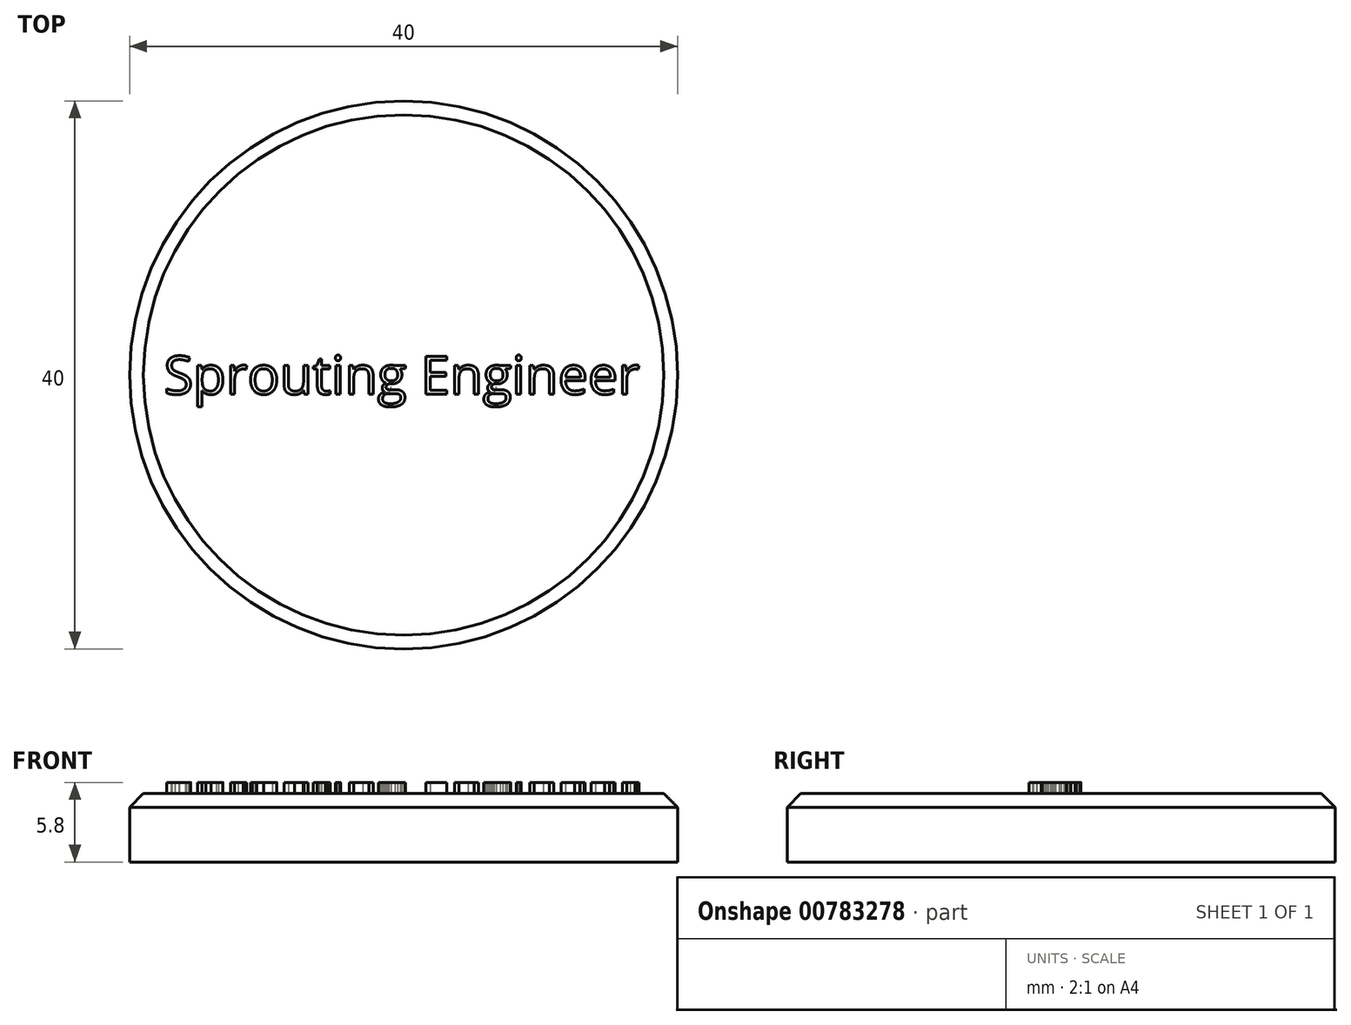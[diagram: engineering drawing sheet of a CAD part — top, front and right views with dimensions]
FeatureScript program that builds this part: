
annotation { "Feature Type Name" : "Feature", "Feature Type Description" : "" }
export const myFeature = defineFeature(function(context is Context, id is Id, definition is map)
    precondition{}
    {
        {
            var Q0;
            Q0=qCreatedBy(makeId("Top.planeOp"),FACE);
            var sketch = newSketch(context, id + "F0", { "sketchPlane" : qUnion([Q0])});
            skCircle(sketch, "E0", {"center": v(0, 0) * mm, "radius": 20 * mm});
            skLineSegment(sketch, "E1", {"start": v(-2.13, 19.89) * mm, "end": v(-1, 23) * mm});
            skLineSegment(sketch, "E2", {"start": v(-1, 23) * mm, "end": v(1, 23) * mm});
            skLineSegment(sketch, "E3", {"start": v(1, 23) * mm, "end": v(2.13, 19.89) * mm});
            skSolve(sketch);
        }
        {
            var Q0;
            {var subQ0=sQuery(id+"F0.wireOp",EDGE,"E0");var subQ1=makeQuery(id+"F0.imprint","INTERSECT",VERTEX,{"derivedFrom":[subQ0,sQuery(id+"F0.wireOp",EDGE,"E1")]});Q0=makeQuery(id+"F0.imprint","IMPRINT",FACE,{"disambiguationData":[TD([[makeQuery(id+"F0.imprint","IMPRINT",EDGE,{"disambiguationData":[TD([[subQ1,1.0]])],"derivedFrom":subQ0}),1.0]])]});}
            var Q1;
            {var subQ0=sQuery(id+"F0.wireOp",EDGE,"E1");Q1=makeQuery(id+"F0.imprint","IMPRINT",FACE,{"disambiguationData":[TD([[makeQuery(id+"F0.imprint","IMPRINT",EDGE,{"derivedFrom":subQ0}),-1.0]])]});}
            extrude(context, id + "F1", {"entities" : qUnion([Q0, Q1]), "depth" : 5 * mm, "offsetDistance" : 25 * mm});
        }
        {
            var Q0;
            Q0=makeQuery(id+"F1.opExtrude","SWEPT_BODY",BODY,{"disambiguationData":[OSD([sQuery(id+"F0.wireOp",EDGE,"E0"),sQuery(id+"F0.wireOp",EDGE,"E1"),sQuery(id+"F0.wireOp",EDGE,"E2"),sQuery(id+"F0.wireOp",EDGE,"E3")])]});
            var Q1;
            Q1=sQuery(id+"F0.wireOp",EDGE,"E0");
            circularPattern(context, id + "F2", {"operationType" : NewBodyOperationType.ADD, "entities" : qUnion([Q0]), "axis" : qUnion([Q1]), "angle" : 360 * degree, "instanceCount" : 18, "equalSpace" : true});
        }
        {
            var Q0;
            Q0=makeQuery(id+"F1.opExtrude","CAP_FACE",FACE,{"disambiguationData":[OSD([sQuery(id+"F0.wireOp",EDGE,"E0"),sQuery(id+"F0.wireOp",EDGE,"E1"),sQuery(id+"F0.wireOp",EDGE,"E2"),sQuery(id+"F0.wireOp",EDGE,"E3")])],"isStart":false});
            var sketch = newSketch(context, id + "F3", { "sketchPlane" : qUnion([Q0])});
            skText(sketch, "E4", { "text": "Sprouting Engineer", "fontName": "OpenSans-Regular.ttf"});
            const initialGuessF3  = {"E4": [-0.0175, -0.0014, 1, 0, 0.0028]};
            skSetInitialGuess(sketch, initialGuessF3);
            skSolve(sketch);
        }
        {
            var Q0;
            Q0=qSketchRegion(id+"F3",true);
            extrude(context, id + "F4", {"entities" : qUnion([Q0]), "operationType" : NewBodyOperationType.ADD, "depth" : 0.8 * mm, "offsetDistance" : 25 * mm});
        }
        {
            var Q0;
            {var subQ1=sQuery(id+"F0.wireOp",EDGE,"E1");var subQ2=sQuery(id+"F0.wireOp",EDGE,"E0");Q0=makeQuery(id+"F2.boolean.opBoolean","SPLIT",EDGE,{"disambiguationData":[TD([makeQuery(id+"F2.opPattern","COPY",FACE,{"derivedFrom":makeQuery(id+"F1.opExtrude","SWEPT_FACE",FACE,{"disambiguationData":[OSD([subQ1])]}),"instanceName":"12"})])],"derivedFrom":makeQuery(id+"F1.opExtrude","CAP_EDGE",EDGE,{"disambiguationData":[OSD([subQ2])],"isStart":false})});}
            var Q1;
            Q1=makeQuery(id+"F2.opPattern","COPY",EDGE,{"derivedFrom":makeQuery(id+"F1.opExtrude","CAP_EDGE",EDGE,{"disambiguationData":[OSD([sQuery(id+"F0.wireOp",EDGE,"E1")])],"isStart":false}),"instanceName":"12"});
            var Q2;
            Q2=makeQuery(id+"F2.opPattern","COPY",EDGE,{"derivedFrom":makeQuery(id+"F1.opExtrude","CAP_EDGE",EDGE,{"disambiguationData":[OSD([sQuery(id+"F0.wireOp",EDGE,"E2")])],"isStart":false}),"instanceName":"12"});
            var Q3;
            Q3=makeQuery(id+"F2.opPattern","COPY",EDGE,{"derivedFrom":makeQuery(id+"F1.opExtrude","CAP_EDGE",EDGE,{"disambiguationData":[OSD([sQuery(id+"F0.wireOp",EDGE,"E3")])],"isStart":false}),"instanceName":"12"});
            var Q4;
            {var subQ1=sQuery(id+"F0.wireOp",EDGE,"E1");var subQ2=sQuery(id+"F0.wireOp",EDGE,"E0");Q4=makeQuery(id+"F2.boolean.opBoolean","SPLIT",EDGE,{"disambiguationData":[TD([makeQuery(id+"F2.opPattern","COPY",FACE,{"derivedFrom":makeQuery(id+"F1.opExtrude","SWEPT_FACE",FACE,{"disambiguationData":[OSD([subQ1])]}),"instanceName":"11"})])],"derivedFrom":makeQuery(id+"F1.opExtrude","CAP_EDGE",EDGE,{"disambiguationData":[OSD([subQ2])],"isStart":false})});}
            var Q5;
            Q5=makeQuery(id+"F2.opPattern","COPY",EDGE,{"derivedFrom":makeQuery(id+"F1.opExtrude","CAP_EDGE",EDGE,{"disambiguationData":[OSD([sQuery(id+"F0.wireOp",EDGE,"E1")])],"isStart":false}),"instanceName":"11"});
            var Q6;
            Q6=makeQuery(id+"F2.opPattern","COPY",EDGE,{"derivedFrom":makeQuery(id+"F1.opExtrude","CAP_EDGE",EDGE,{"disambiguationData":[OSD([sQuery(id+"F0.wireOp",EDGE,"E2")])],"isStart":false}),"instanceName":"11"});
            var Q7;
            Q7=makeQuery(id+"F2.opPattern","COPY",EDGE,{"derivedFrom":makeQuery(id+"F1.opExtrude","CAP_EDGE",EDGE,{"disambiguationData":[OSD([sQuery(id+"F0.wireOp",EDGE,"E3")])],"isStart":false}),"instanceName":"11"});
            var Q8;
            Q8=makeQuery(id+"F2.opPattern","COPY",EDGE,{"derivedFrom":makeQuery(id+"F1.opExtrude","CAP_EDGE",EDGE,{"disambiguationData":[OSD([sQuery(id+"F0.wireOp",EDGE,"E3")])],"isStart":false}),"instanceName":"13"});
            var Q9;
            Q9=makeQuery(id+"F2.opPattern","COPY",EDGE,{"derivedFrom":makeQuery(id+"F1.opExtrude","CAP_EDGE",EDGE,{"disambiguationData":[OSD([sQuery(id+"F0.wireOp",EDGE,"E2")])],"isStart":false}),"instanceName":"13"});
            var Q10;
            Q10=makeQuery(id+"F2.opPattern","COPY",EDGE,{"derivedFrom":makeQuery(id+"F1.opExtrude","CAP_EDGE",EDGE,{"disambiguationData":[OSD([sQuery(id+"F0.wireOp",EDGE,"E1")])],"isStart":false}),"instanceName":"13"});
            var Q11;
            {var subQ1=sQuery(id+"F0.wireOp",EDGE,"E1");var subQ2=sQuery(id+"F0.wireOp",EDGE,"E0");Q11=makeQuery(id+"F2.boolean.opBoolean","SPLIT",EDGE,{"disambiguationData":[TD([makeQuery(id+"F2.opPattern","COPY",FACE,{"derivedFrom":makeQuery(id+"F1.opExtrude","SWEPT_FACE",FACE,{"disambiguationData":[OSD([subQ1])]}),"instanceName":"13"})])],"derivedFrom":makeQuery(id+"F1.opExtrude","CAP_EDGE",EDGE,{"disambiguationData":[OSD([subQ2])],"isStart":false})});}
            var Q12;
            Q12=makeQuery(id+"F2.opPattern","COPY",EDGE,{"derivedFrom":makeQuery(id+"F1.opExtrude","CAP_EDGE",EDGE,{"disambiguationData":[OSD([sQuery(id+"F0.wireOp",EDGE,"E3")])],"isStart":false}),"instanceName":"14"});
            var Q13;
            Q13=makeQuery(id+"F2.opPattern","COPY",EDGE,{"derivedFrom":makeQuery(id+"F1.opExtrude","CAP_EDGE",EDGE,{"disambiguationData":[OSD([sQuery(id+"F0.wireOp",EDGE,"E2")])],"isStart":false}),"instanceName":"14"});
            var Q14;
            Q14=makeQuery(id+"F2.opPattern","COPY",EDGE,{"derivedFrom":makeQuery(id+"F1.opExtrude","CAP_EDGE",EDGE,{"disambiguationData":[OSD([sQuery(id+"F0.wireOp",EDGE,"E1")])],"isStart":false}),"instanceName":"14"});
            var Q15;
            {var subQ1=sQuery(id+"F0.wireOp",EDGE,"E1");var subQ2=sQuery(id+"F0.wireOp",EDGE,"E0");Q15=makeQuery(id+"F2.boolean.opBoolean","SPLIT",EDGE,{"disambiguationData":[TD([makeQuery(id+"F2.opPattern","COPY",FACE,{"derivedFrom":makeQuery(id+"F1.opExtrude","SWEPT_FACE",FACE,{"disambiguationData":[OSD([subQ1])]}),"instanceName":"14"})])],"derivedFrom":makeQuery(id+"F1.opExtrude","CAP_EDGE",EDGE,{"disambiguationData":[OSD([subQ2])],"isStart":false})});}
            var Q16;
            Q16=makeQuery(id+"F2.opPattern","COPY",EDGE,{"derivedFrom":makeQuery(id+"F1.opExtrude","CAP_EDGE",EDGE,{"disambiguationData":[OSD([sQuery(id+"F0.wireOp",EDGE,"E3")])],"isStart":false}),"instanceName":"15"});
            var Q17;
            Q17=makeQuery(id+"F2.opPattern","COPY",EDGE,{"derivedFrom":makeQuery(id+"F1.opExtrude","CAP_EDGE",EDGE,{"disambiguationData":[OSD([sQuery(id+"F0.wireOp",EDGE,"E2")])],"isStart":false}),"instanceName":"15"});
            var Q18;
            Q18=makeQuery(id+"F2.opPattern","COPY",EDGE,{"derivedFrom":makeQuery(id+"F1.opExtrude","CAP_EDGE",EDGE,{"disambiguationData":[OSD([sQuery(id+"F0.wireOp",EDGE,"E1")])],"isStart":false}),"instanceName":"15"});
            var Q19;
            {var subQ1=sQuery(id+"F0.wireOp",EDGE,"E1");var subQ2=sQuery(id+"F0.wireOp",EDGE,"E0");Q19=makeQuery(id+"F2.boolean.opBoolean","SPLIT",EDGE,{"disambiguationData":[TD([makeQuery(id+"F2.opPattern","COPY",FACE,{"derivedFrom":makeQuery(id+"F1.opExtrude","SWEPT_FACE",FACE,{"disambiguationData":[OSD([subQ1])]}),"instanceName":"15"})])],"derivedFrom":makeQuery(id+"F1.opExtrude","CAP_EDGE",EDGE,{"disambiguationData":[OSD([subQ2])],"isStart":false})});}
            var Q20;
            Q20=makeQuery(id+"F2.opPattern","COPY",EDGE,{"derivedFrom":makeQuery(id+"F1.opExtrude","CAP_EDGE",EDGE,{"disambiguationData":[OSD([sQuery(id+"F0.wireOp",EDGE,"E3")])],"isStart":false}),"instanceName":"16"});
            var Q21;
            Q21=makeQuery(id+"F2.opPattern","COPY",EDGE,{"derivedFrom":makeQuery(id+"F1.opExtrude","CAP_EDGE",EDGE,{"disambiguationData":[OSD([sQuery(id+"F0.wireOp",EDGE,"E2")])],"isStart":false}),"instanceName":"16"});
            var Q22;
            Q22=makeQuery(id+"F2.opPattern","COPY",EDGE,{"derivedFrom":makeQuery(id+"F1.opExtrude","CAP_EDGE",EDGE,{"disambiguationData":[OSD([sQuery(id+"F0.wireOp",EDGE,"E1")])],"isStart":false}),"instanceName":"16"});
            var Q23;
            {var subQ1=sQuery(id+"F0.wireOp",EDGE,"E1");var subQ2=sQuery(id+"F0.wireOp",EDGE,"E0");Q23=makeQuery(id+"F2.boolean.opBoolean","SPLIT",EDGE,{"disambiguationData":[TD([makeQuery(id+"F2.opPattern","COPY",FACE,{"derivedFrom":makeQuery(id+"F1.opExtrude","SWEPT_FACE",FACE,{"disambiguationData":[OSD([subQ1])]}),"instanceName":"16"})])],"derivedFrom":makeQuery(id+"F1.opExtrude","CAP_EDGE",EDGE,{"disambiguationData":[OSD([subQ2])],"isStart":false})});}
            var Q24;
            Q24=makeQuery(id+"F2.opPattern","COPY",EDGE,{"derivedFrom":makeQuery(id+"F1.opExtrude","CAP_EDGE",EDGE,{"disambiguationData":[OSD([sQuery(id+"F0.wireOp",EDGE,"E3")])],"isStart":false}),"instanceName":"17"});
            var Q25;
            Q25=makeQuery(id+"F2.opPattern","COPY",EDGE,{"derivedFrom":makeQuery(id+"F1.opExtrude","CAP_EDGE",EDGE,{"disambiguationData":[OSD([sQuery(id+"F0.wireOp",EDGE,"E1")])],"isStart":false}),"instanceName":"17"});
            var Q26;
            {var subQ0=sQuery(id+"F0.wireOp",EDGE,"E3");var subQ2=sQuery(id+"F0.wireOp",EDGE,"E0");Q26=makeQuery(id+"F2.boolean.opBoolean","SPLIT",EDGE,{"disambiguationData":[TD([makeQuery(id+"F1.opExtrude","SWEPT_FACE",FACE,{"disambiguationData":[OSD([subQ0])]})])],"derivedFrom":makeQuery(id+"F1.opExtrude","CAP_EDGE",EDGE,{"disambiguationData":[OSD([subQ2])],"isStart":false})});}
            var Q27;
            Q27=makeQuery(id+"F1.opExtrude","CAP_EDGE",EDGE,{"disambiguationData":[OSD([sQuery(id+"F0.wireOp",EDGE,"E3")])],"isStart":false});
            var Q28;
            Q28=makeQuery(id+"F1.opExtrude","CAP_EDGE",EDGE,{"disambiguationData":[OSD([sQuery(id+"F0.wireOp",EDGE,"E1")])],"isStart":false});
            var Q29;
            {var subQ1=sQuery(id+"F0.wireOp",EDGE,"E1");var subQ2=sQuery(id+"F0.wireOp",EDGE,"E0");Q29=makeQuery(id+"F2.boolean.opBoolean","SPLIT",EDGE,{"disambiguationData":[TD([makeQuery(id+"F1.opExtrude","SWEPT_FACE",FACE,{"disambiguationData":[OSD([subQ1])]})])],"derivedFrom":makeQuery(id+"F1.opExtrude","CAP_EDGE",EDGE,{"disambiguationData":[OSD([subQ2])],"isStart":false})});}
            var Q30;
            Q30=makeQuery(id+"F2.opPattern","COPY",EDGE,{"derivedFrom":makeQuery(id+"F1.opExtrude","CAP_EDGE",EDGE,{"disambiguationData":[OSD([sQuery(id+"F0.wireOp",EDGE,"E3")])],"isStart":false}),"instanceName":"1"});
            var Q31;
            Q31=makeQuery(id+"F2.opPattern","COPY",EDGE,{"derivedFrom":makeQuery(id+"F1.opExtrude","CAP_EDGE",EDGE,{"disambiguationData":[OSD([sQuery(id+"F0.wireOp",EDGE,"E1")])],"isStart":false}),"instanceName":"1"});
            var Q32;
            {var subQ1=sQuery(id+"F0.wireOp",EDGE,"E1");var subQ2=sQuery(id+"F0.wireOp",EDGE,"E0");Q32=makeQuery(id+"F2.boolean.opBoolean","SPLIT",EDGE,{"disambiguationData":[TD([makeQuery(id+"F2.opPattern","COPY",FACE,{"derivedFrom":makeQuery(id+"F1.opExtrude","SWEPT_FACE",FACE,{"disambiguationData":[OSD([subQ1])]}),"instanceName":"1"})])],"derivedFrom":makeQuery(id+"F1.opExtrude","CAP_EDGE",EDGE,{"disambiguationData":[OSD([subQ2])],"isStart":false})});}
            var Q33;
            Q33=makeQuery(id+"F2.opPattern","COPY",EDGE,{"derivedFrom":makeQuery(id+"F1.opExtrude","CAP_EDGE",EDGE,{"disambiguationData":[OSD([sQuery(id+"F0.wireOp",EDGE,"E3")])],"isStart":false}),"instanceName":"2"});
            var Q34;
            Q34=makeQuery(id+"F2.opPattern","COPY",EDGE,{"derivedFrom":makeQuery(id+"F1.opExtrude","CAP_EDGE",EDGE,{"disambiguationData":[OSD([sQuery(id+"F0.wireOp",EDGE,"E1")])],"isStart":false}),"instanceName":"2"});
            var Q35;
            {var subQ1=sQuery(id+"F0.wireOp",EDGE,"E1");var subQ2=sQuery(id+"F0.wireOp",EDGE,"E0");Q35=makeQuery(id+"F2.boolean.opBoolean","SPLIT",EDGE,{"disambiguationData":[TD([makeQuery(id+"F2.opPattern","COPY",FACE,{"derivedFrom":makeQuery(id+"F1.opExtrude","SWEPT_FACE",FACE,{"disambiguationData":[OSD([subQ1])]}),"instanceName":"2"})])],"derivedFrom":makeQuery(id+"F1.opExtrude","CAP_EDGE",EDGE,{"disambiguationData":[OSD([subQ2])],"isStart":false})});}
            var Q36;
            Q36=makeQuery(id+"F2.opPattern","COPY",EDGE,{"derivedFrom":makeQuery(id+"F1.opExtrude","CAP_EDGE",EDGE,{"disambiguationData":[OSD([sQuery(id+"F0.wireOp",EDGE,"E3")])],"isStart":false}),"instanceName":"3"});
            var Q37;
            Q37=makeQuery(id+"F2.opPattern","COPY",EDGE,{"derivedFrom":makeQuery(id+"F1.opExtrude","CAP_EDGE",EDGE,{"disambiguationData":[OSD([sQuery(id+"F0.wireOp",EDGE,"E1")])],"isStart":false}),"instanceName":"3"});
            var Q38;
            {var subQ1=sQuery(id+"F0.wireOp",EDGE,"E1");var subQ2=sQuery(id+"F0.wireOp",EDGE,"E0");Q38=makeQuery(id+"F2.boolean.opBoolean","SPLIT",EDGE,{"disambiguationData":[TD([makeQuery(id+"F2.opPattern","COPY",FACE,{"derivedFrom":makeQuery(id+"F1.opExtrude","SWEPT_FACE",FACE,{"disambiguationData":[OSD([subQ1])]}),"instanceName":"3"})])],"derivedFrom":makeQuery(id+"F1.opExtrude","CAP_EDGE",EDGE,{"disambiguationData":[OSD([subQ2])],"isStart":false})});}
            var Q39;
            Q39=makeQuery(id+"F2.opPattern","COPY",EDGE,{"derivedFrom":makeQuery(id+"F1.opExtrude","CAP_EDGE",EDGE,{"disambiguationData":[OSD([sQuery(id+"F0.wireOp",EDGE,"E3")])],"isStart":false}),"instanceName":"4"});
            var Q40;
            Q40=makeQuery(id+"F2.opPattern","COPY",EDGE,{"derivedFrom":makeQuery(id+"F1.opExtrude","CAP_EDGE",EDGE,{"disambiguationData":[OSD([sQuery(id+"F0.wireOp",EDGE,"E2")])],"isStart":false}),"instanceName":"4"});
            var Q41;
            Q41=makeQuery(id+"F2.opPattern","COPY",EDGE,{"derivedFrom":makeQuery(id+"F1.opExtrude","CAP_EDGE",EDGE,{"disambiguationData":[OSD([sQuery(id+"F0.wireOp",EDGE,"E1")])],"isStart":false}),"instanceName":"4"});
            var Q42;
            Q42=makeQuery(id+"F2.opPattern","COPY",EDGE,{"derivedFrom":makeQuery(id+"F1.opExtrude","CAP_EDGE",EDGE,{"disambiguationData":[OSD([sQuery(id+"F0.wireOp",EDGE,"E2")])],"isStart":false}),"instanceName":"3"});
            var Q43;
            Q43=makeQuery(id+"F2.opPattern","COPY",EDGE,{"derivedFrom":makeQuery(id+"F1.opExtrude","CAP_EDGE",EDGE,{"disambiguationData":[OSD([sQuery(id+"F0.wireOp",EDGE,"E2")])],"isStart":false}),"instanceName":"2"});
            var Q44;
            Q44=makeQuery(id+"F2.opPattern","COPY",EDGE,{"derivedFrom":makeQuery(id+"F1.opExtrude","CAP_EDGE",EDGE,{"disambiguationData":[OSD([sQuery(id+"F0.wireOp",EDGE,"E2")])],"isStart":false}),"instanceName":"1"});
            var Q45;
            Q45=makeQuery(id+"F1.opExtrude","CAP_EDGE",EDGE,{"disambiguationData":[OSD([sQuery(id+"F0.wireOp",EDGE,"E2")])],"isStart":false});
            var Q46;
            Q46=makeQuery(id+"F2.opPattern","COPY",EDGE,{"derivedFrom":makeQuery(id+"F1.opExtrude","CAP_EDGE",EDGE,{"disambiguationData":[OSD([sQuery(id+"F0.wireOp",EDGE,"E2")])],"isStart":false}),"instanceName":"17"});
            var Q47;
            {var subQ1=sQuery(id+"F0.wireOp",EDGE,"E1");var subQ2=sQuery(id+"F0.wireOp",EDGE,"E0");Q47=makeQuery(id+"F2.boolean.opBoolean","SPLIT",EDGE,{"disambiguationData":[TD([makeQuery(id+"F2.opPattern","COPY",FACE,{"derivedFrom":makeQuery(id+"F1.opExtrude","SWEPT_FACE",FACE,{"disambiguationData":[OSD([subQ1])]}),"instanceName":"4"})])],"derivedFrom":makeQuery(id+"F1.opExtrude","CAP_EDGE",EDGE,{"disambiguationData":[OSD([subQ2])],"isStart":false})});}
            var Q48;
            Q48=makeQuery(id+"F2.opPattern","COPY",EDGE,{"derivedFrom":makeQuery(id+"F1.opExtrude","CAP_EDGE",EDGE,{"disambiguationData":[OSD([sQuery(id+"F0.wireOp",EDGE,"E3")])],"isStart":false}),"instanceName":"5"});
            var Q49;
            Q49=makeQuery(id+"F2.opPattern","COPY",EDGE,{"derivedFrom":makeQuery(id+"F1.opExtrude","CAP_EDGE",EDGE,{"disambiguationData":[OSD([sQuery(id+"F0.wireOp",EDGE,"E2")])],"isStart":false}),"instanceName":"5"});
            var Q50;
            Q50=makeQuery(id+"F2.opPattern","COPY",EDGE,{"derivedFrom":makeQuery(id+"F1.opExtrude","CAP_EDGE",EDGE,{"disambiguationData":[OSD([sQuery(id+"F0.wireOp",EDGE,"E1")])],"isStart":false}),"instanceName":"5"});
            var Q51;
            {var subQ1=sQuery(id+"F0.wireOp",EDGE,"E1");var subQ2=sQuery(id+"F0.wireOp",EDGE,"E0");Q51=makeQuery(id+"F2.boolean.opBoolean","SPLIT",EDGE,{"disambiguationData":[TD([makeQuery(id+"F2.opPattern","COPY",FACE,{"derivedFrom":makeQuery(id+"F1.opExtrude","SWEPT_FACE",FACE,{"disambiguationData":[OSD([subQ1])]}),"instanceName":"5"})])],"derivedFrom":makeQuery(id+"F1.opExtrude","CAP_EDGE",EDGE,{"disambiguationData":[OSD([subQ2])],"isStart":false})});}
            var Q52;
            Q52=makeQuery(id+"F2.opPattern","COPY",EDGE,{"derivedFrom":makeQuery(id+"F1.opExtrude","CAP_EDGE",EDGE,{"disambiguationData":[OSD([sQuery(id+"F0.wireOp",EDGE,"E3")])],"isStart":false}),"instanceName":"6"});
            var Q53;
            Q53=makeQuery(id+"F2.opPattern","COPY",EDGE,{"derivedFrom":makeQuery(id+"F1.opExtrude","CAP_EDGE",EDGE,{"disambiguationData":[OSD([sQuery(id+"F0.wireOp",EDGE,"E2")])],"isStart":false}),"instanceName":"6"});
            var Q54;
            Q54=makeQuery(id+"F2.opPattern","COPY",EDGE,{"derivedFrom":makeQuery(id+"F1.opExtrude","CAP_EDGE",EDGE,{"disambiguationData":[OSD([sQuery(id+"F0.wireOp",EDGE,"E1")])],"isStart":false}),"instanceName":"6"});
            var Q55;
            {var subQ1=sQuery(id+"F0.wireOp",EDGE,"E1");var subQ2=sQuery(id+"F0.wireOp",EDGE,"E0");Q55=makeQuery(id+"F2.boolean.opBoolean","SPLIT",EDGE,{"disambiguationData":[TD([makeQuery(id+"F2.opPattern","COPY",FACE,{"derivedFrom":makeQuery(id+"F1.opExtrude","SWEPT_FACE",FACE,{"disambiguationData":[OSD([subQ1])]}),"instanceName":"6"})])],"derivedFrom":makeQuery(id+"F1.opExtrude","CAP_EDGE",EDGE,{"disambiguationData":[OSD([subQ2])],"isStart":false})});}
            var Q56;
            Q56=makeQuery(id+"F2.opPattern","COPY",EDGE,{"derivedFrom":makeQuery(id+"F1.opExtrude","CAP_EDGE",EDGE,{"disambiguationData":[OSD([sQuery(id+"F0.wireOp",EDGE,"E3")])],"isStart":false}),"instanceName":"7"});
            var Q57;
            Q57=makeQuery(id+"F2.opPattern","COPY",EDGE,{"derivedFrom":makeQuery(id+"F1.opExtrude","CAP_EDGE",EDGE,{"disambiguationData":[OSD([sQuery(id+"F0.wireOp",EDGE,"E2")])],"isStart":false}),"instanceName":"7"});
            var Q58;
            Q58=makeQuery(id+"F2.opPattern","COPY",EDGE,{"derivedFrom":makeQuery(id+"F1.opExtrude","CAP_EDGE",EDGE,{"disambiguationData":[OSD([sQuery(id+"F0.wireOp",EDGE,"E1")])],"isStart":false}),"instanceName":"7"});
            var Q59;
            {var subQ0=sQuery(id+"F0.wireOp",EDGE,"E1");var subQ2=sQuery(id+"F0.wireOp",EDGE,"E0");Q59=makeQuery(id+"F2.boolean.opBoolean","SPLIT",EDGE,{"disambiguationData":[TD([makeQuery(id+"F2.opPattern","COPY",FACE,{"derivedFrom":makeQuery(id+"F1.opExtrude","SWEPT_FACE",FACE,{"disambiguationData":[OSD([subQ0])]}),"instanceName":"7"})])],"derivedFrom":makeQuery(id+"F1.opExtrude","CAP_EDGE",EDGE,{"disambiguationData":[OSD([subQ2])],"isStart":false})});}
            var Q60;
            Q60=makeQuery(id+"F2.opPattern","COPY",EDGE,{"derivedFrom":makeQuery(id+"F1.opExtrude","CAP_EDGE",EDGE,{"disambiguationData":[OSD([sQuery(id+"F0.wireOp",EDGE,"E3")])],"isStart":false}),"instanceName":"8"});
            var Q61;
            Q61=makeQuery(id+"F2.opPattern","COPY",EDGE,{"derivedFrom":makeQuery(id+"F1.opExtrude","CAP_EDGE",EDGE,{"disambiguationData":[OSD([sQuery(id+"F0.wireOp",EDGE,"E2")])],"isStart":false}),"instanceName":"8"});
            var Q62;
            Q62=makeQuery(id+"F2.opPattern","COPY",EDGE,{"derivedFrom":makeQuery(id+"F1.opExtrude","CAP_EDGE",EDGE,{"disambiguationData":[OSD([sQuery(id+"F0.wireOp",EDGE,"E1")])],"isStart":false}),"instanceName":"8"});
            var Q63;
            {var subQ1=sQuery(id+"F0.wireOp",EDGE,"E1");var subQ2=sQuery(id+"F0.wireOp",EDGE,"E0");Q63=makeQuery(id+"F2.boolean.opBoolean","SPLIT",EDGE,{"disambiguationData":[TD([makeQuery(id+"F2.opPattern","COPY",FACE,{"derivedFrom":makeQuery(id+"F1.opExtrude","SWEPT_FACE",FACE,{"disambiguationData":[OSD([subQ1])]}),"instanceName":"8"})])],"derivedFrom":makeQuery(id+"F1.opExtrude","CAP_EDGE",EDGE,{"disambiguationData":[OSD([subQ2])],"isStart":false})});}
            var Q64;
            Q64=makeQuery(id+"F2.opPattern","COPY",EDGE,{"derivedFrom":makeQuery(id+"F1.opExtrude","CAP_EDGE",EDGE,{"disambiguationData":[OSD([sQuery(id+"F0.wireOp",EDGE,"E3")])],"isStart":false}),"instanceName":"9"});
            var Q65;
            Q65=makeQuery(id+"F2.opPattern","COPY",EDGE,{"derivedFrom":makeQuery(id+"F1.opExtrude","CAP_EDGE",EDGE,{"disambiguationData":[OSD([sQuery(id+"F0.wireOp",EDGE,"E2")])],"isStart":false}),"instanceName":"9"});
            var Q66;
            Q66=makeQuery(id+"F2.opPattern","COPY",EDGE,{"derivedFrom":makeQuery(id+"F1.opExtrude","CAP_EDGE",EDGE,{"disambiguationData":[OSD([sQuery(id+"F0.wireOp",EDGE,"E1")])],"isStart":false}),"instanceName":"9"});
            var Q67;
            {var subQ1=sQuery(id+"F0.wireOp",EDGE,"E1");var subQ2=sQuery(id+"F0.wireOp",EDGE,"E0");Q67=makeQuery(id+"F2.boolean.opBoolean","SPLIT",EDGE,{"disambiguationData":[TD([makeQuery(id+"F2.opPattern","COPY",FACE,{"derivedFrom":makeQuery(id+"F1.opExtrude","SWEPT_FACE",FACE,{"disambiguationData":[OSD([subQ1])]}),"instanceName":"9"})])],"derivedFrom":makeQuery(id+"F1.opExtrude","CAP_EDGE",EDGE,{"disambiguationData":[OSD([subQ2])],"isStart":false})});}
            var Q68;
            Q68=makeQuery(id+"F2.opPattern","COPY",EDGE,{"derivedFrom":makeQuery(id+"F1.opExtrude","CAP_EDGE",EDGE,{"disambiguationData":[OSD([sQuery(id+"F0.wireOp",EDGE,"E3")])],"isStart":false}),"instanceName":"10"});
            var Q69;
            Q69=makeQuery(id+"F2.opPattern","COPY",EDGE,{"derivedFrom":makeQuery(id+"F1.opExtrude","CAP_EDGE",EDGE,{"disambiguationData":[OSD([sQuery(id+"F0.wireOp",EDGE,"E2")])],"isStart":false}),"instanceName":"10"});
            var Q70;
            Q70=makeQuery(id+"F2.opPattern","COPY",EDGE,{"derivedFrom":makeQuery(id+"F1.opExtrude","CAP_EDGE",EDGE,{"disambiguationData":[OSD([sQuery(id+"F0.wireOp",EDGE,"E1")])],"isStart":false}),"instanceName":"10"});
            var Q71;
            {var subQ1=sQuery(id+"F0.wireOp",EDGE,"E1");var subQ2=sQuery(id+"F0.wireOp",EDGE,"E0");Q71=makeQuery(id+"F2.boolean.opBoolean","SPLIT",EDGE,{"disambiguationData":[TD([makeQuery(id+"F2.opPattern","COPY",FACE,{"derivedFrom":makeQuery(id+"F1.opExtrude","SWEPT_FACE",FACE,{"disambiguationData":[OSD([subQ1])]}),"instanceName":"10"})])],"derivedFrom":makeQuery(id+"F1.opExtrude","CAP_EDGE",EDGE,{"disambiguationData":[OSD([subQ2])],"isStart":false})});}
            chamfer(context, id + "F5", {"entities" : qUnion([Q0, Q1, Q2, Q3, Q4, Q5, Q6, Q7, Q8, Q9, Q10, Q11, Q12, Q13, Q14, Q15, Q16, Q17, Q18, Q19, Q20, Q21, Q22, Q23, Q24, Q25, Q26, Q27, Q28, Q29, Q30, Q31, Q32, Q33, Q34, Q35, Q36, Q37, Q38, Q39, Q40, Q41, Q42, Q43, Q44, Q45, Q46, Q47, Q48, Q49, Q50, Q51, Q52, Q53, Q54, Q55, Q56, Q57, Q58, Q59, Q60, Q61, Q62, Q63, Q64, Q65, Q66, Q67, Q68, Q69, Q70, Q71]), "width" : 1 * mm, "tangentPropagation" : true});
        }
    });
